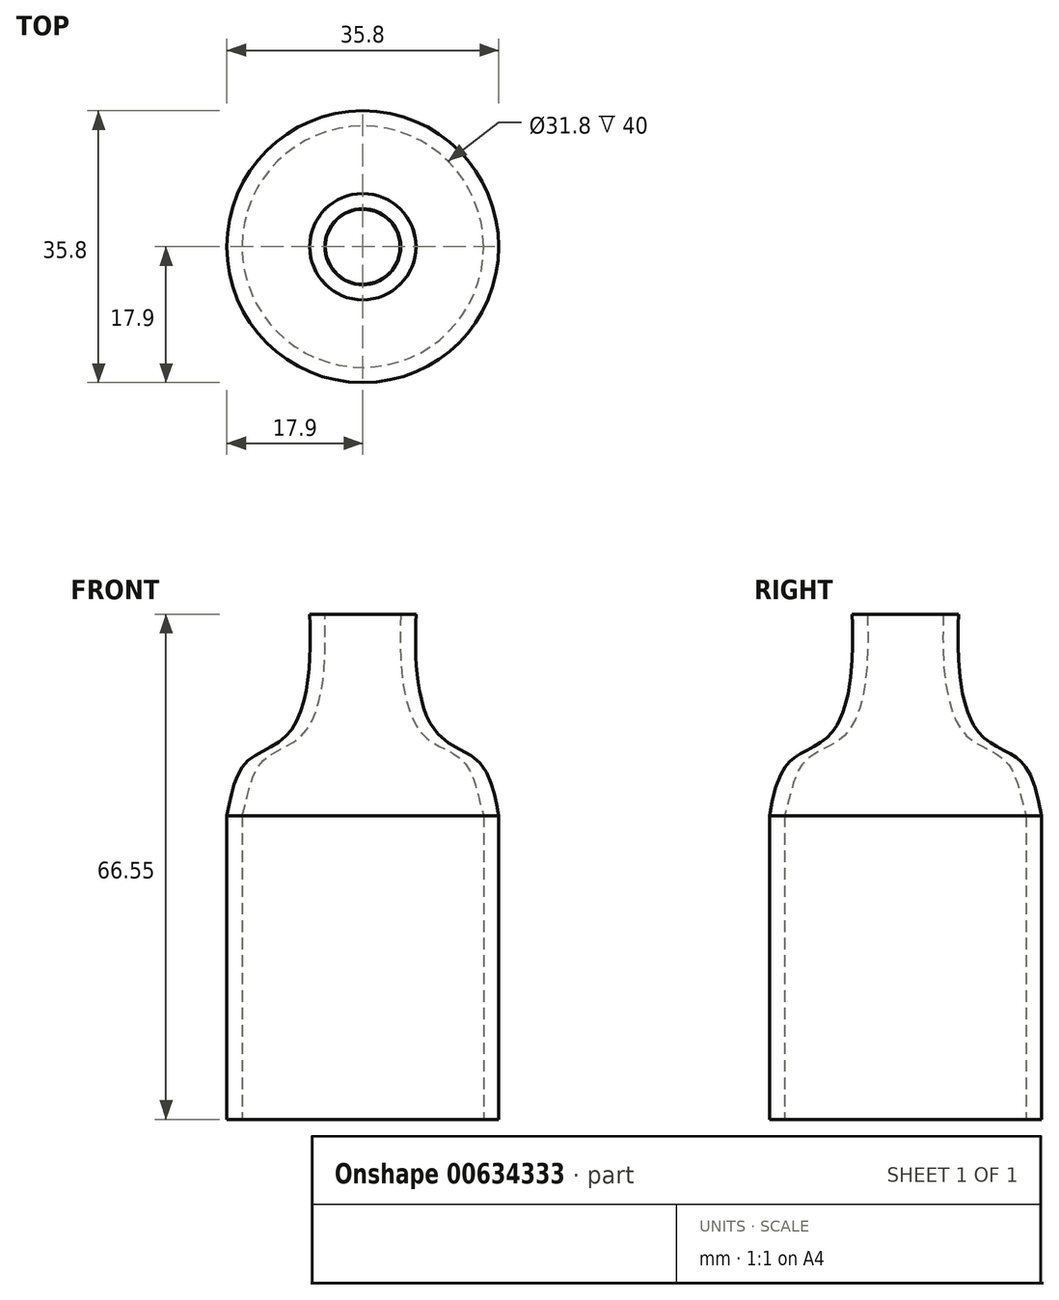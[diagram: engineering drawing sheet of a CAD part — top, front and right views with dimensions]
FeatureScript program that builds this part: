
annotation { "Feature Type Name" : "Feature", "Feature Type Description" : "" }
export const myFeature = defineFeature(function(context is Context, id is Id, definition is map)
    precondition{}
    {
        {
            var Q0;
            Q0=qCreatedBy(makeId("Front.planeOp"),FACE);
            var sketch = newSketch(context, id + "F0", { "sketchPlane" : qUnion([Q0])});
            skLineSegment(sketch, "E0", {"start": v(0, 0) * mm, "end": v(15.9, 0) * mm});
            skLineSegment(sketch, "E1", {"start": v(15.9, 0) * mm, "end": v(15.9, 40) * mm});
            skLineSegment(sketch, "E2", {"start": v(0, 66.55) * mm, "end": v(5, 66.55) * mm, "construction": true});
            skFitSpline(sketch, "E3", {"points": [v(15.9, 40) * mm, v(13.34, 47.04) * mm, v(8.28, 50.32) * mm, v(5.3, 57.47) * mm, v(5, 66.55) * mm], "startDerivative": vector(-8.93, 28.77) * mm, "endDerivative": vector(0.83, 32.71) * mm});
            skLineSegment(sketch, "E4", {"start": v(5, 66.55) * mm, "end": v(0, 66.55) * mm});
            skLineSegment(sketch, "E5", {"start": v(0, 0) * mm, "end": v(0, 66.55) * mm});
            skLineSegment(sketch, "E6", {"start": v(15.9, 0) * mm, "end": v(17.9, 0) * mm});
            skLineSegment(sketch, "E7", {"start": v(17.9, 0) * mm, "end": v(17.9, 40) * mm});
            skLineSegment(sketch, "E8", {"start": v(5.3, 57.47) * mm, "end": v(7.3, 57.47) * mm, "construction": true});
            skLineSegment(sketch, "E9", {"start": v(5, 66.55) * mm, "end": v(7, 66.55) * mm, "construction": true});
            skLineSegment(sketch, "E10", {"start": v(8.28, 50.32) * mm, "end": v(10.28, 50.32) * mm, "construction": true});
            skLineSegment(sketch, "E11", {"start": v(13.34, 47.04) * mm, "end": v(15.34, 47.04) * mm, "construction": true});
            skFitSpline(sketch, "E12", {"points": [v(17.9, 40) * mm, v(15.34, 47.04) * mm, v(10.28, 50.32) * mm, v(7.3, 57.47) * mm, v(7, 66.55) * mm], "startDerivative": vector(-6.23, 32.97) * mm, "endDerivative": vector(0.8, 33.16) * mm});
            skLineSegment(sketch, "E13", {"start": v(5, 66.55) * mm, "end": v(7, 66.55) * mm});
            skSolve(sketch);
        }
        {
            var Q0;
            Q0=makeQuery(id+"F0.imprint","IMPRINT",FACE,{"disambiguationData":[TD([[makeQuery(id+"F0.imprint","IMPRINT",EDGE,{"derivedFrom":sQuery(id+"F0.wireOp",EDGE,"E1")}),-1.0]])]});
            var Q1;
            Q1=sQuery(id+"F0.wireOp",EDGE,"E5");
            revolve(context, id + "F1", {"surfaceOperationType" : NewSurfaceOperationType.NEW, "entities" : qUnion([Q0]), "axis" : qUnion([Q1]), "revolveType" : RevolveType.FULL});
        }
    });
